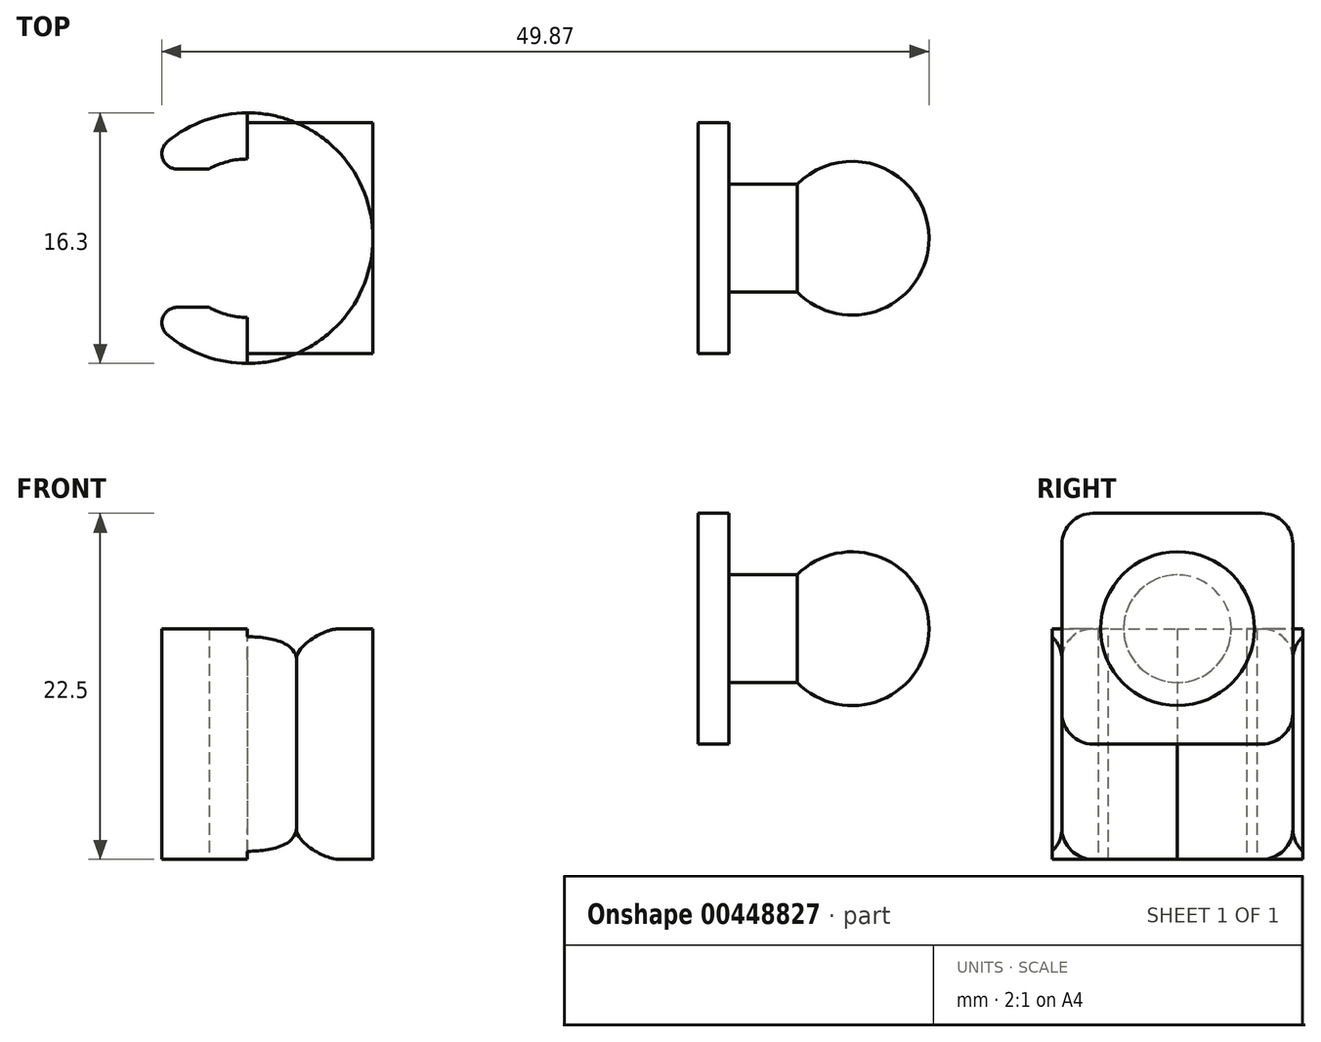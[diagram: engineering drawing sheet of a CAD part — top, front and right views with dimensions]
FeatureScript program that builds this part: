
annotation { "Feature Type Name" : "Feature", "Feature Type Description" : "" }
export const myFeature = defineFeature(function(context is Context, id is Id, definition is map)
    precondition{}
    {
        {
            var Q0;
            Q0=qCreatedBy(makeId("Top.planeOp"),FACE);
            var sketch = newSketch(context, id + "F0", { "sketchPlane" : qUnion([Q0])});
            skLineSegment(sketch, "E0.bottom", {"start": v(0, 0) * mm, "end": v(-8.15, 0) * mm});
            skLineSegment(sketch, "E0.top", {"start": v(0, 15) * mm, "end": v(-8.15, 15) * mm});
            skLineSegment(sketch, "E0.left", {"start": v(0, 0) * mm, "end": v(0, 15) * mm});
            skLineSegment(sketch, "E0.right", {"start": v(-8.15, 0) * mm, "end": v(-8.15, 15) * mm});
            skCircle(sketch, "E1", {"center": v(-8.15, 7.5) * mm, "radius": 8.15 * mm});
            skPoint(sketch, "E1.centerSnap0", {"position": v(-8.15, 7.5) * mm});
            skCircle(sketch, "E2", {"center": v(-8.15, 7.5) * mm, "radius": 5.15 * mm});
            skLineSegment(sketch, "E3.bottom", {"start": v(-22.3, 12) * mm, "end": v(-10.3, 12) * mm});
            skLineSegment(sketch, "E3.top", {"start": v(-22.3, 3) * mm, "end": v(-10.3, 3) * mm});
            skLineSegment(sketch, "E3.left", {"start": v(-22.3, 12) * mm, "end": v(-22.3, 3) * mm});
            skLineSegment(sketch, "E3.right", {"start": v(-10.3, 12) * mm, "end": v(-10.3, 3) * mm});
            skPoint(sketch, "E3.middle", {"position": v(-16.3, 7.5) * mm});
            skSolve(sketch);
        }
        {
            var Q0;
            {var subQ1=sQuery(id+"F0.wireOp",EDGE,"E0.right");var subQ6=sQuery(id+"F0.wireOp",EDGE,"E0.top");var subQ9=makeQuery(id+"F0.imprint","INTERSECT",VERTEX,{"derivedFrom":[subQ6,subQ1]});Q0=makeQuery(id+"F0.imprint","IMPRINT",FACE,{"disambiguationData":[TD([[makeQuery(id+"F0.imprint","IMPRINT",EDGE,{"disambiguationData":[TD([[subQ9,1.0]])],"derivedFrom":subQ6}),-1.0]])]});}
            var Q1;
            {var subQ3=sQuery(id+"F0.wireOp",EDGE,"E2");var subQ6=makeQuery(id+"F0.imprint","IMPRINT",VERTEX,{"derivedFrom":subQ3});Q1=makeQuery(id+"F0.imprint","IMPRINT",FACE,{"disambiguationData":[TD([[makeQuery(id+"F0.imprint","IMPRINT",EDGE,{"disambiguationData":[TD([[subQ6,-1.0]])],"derivedFrom":subQ3}),-1.0]])]});}
            var Q2;
            {var subQ1=sQuery(id+"F0.wireOp",EDGE,"E0.right");var subQ6=sQuery(id+"F0.wireOp",EDGE,"E0.bottom");var subQ9=makeQuery(id+"F0.imprint","INTERSECT",VERTEX,{"derivedFrom":[subQ6,subQ1]});Q2=makeQuery(id+"F0.imprint","IMPRINT",FACE,{"disambiguationData":[TD([[makeQuery(id+"F0.imprint","IMPRINT",EDGE,{"disambiguationData":[TD([[subQ9,1.0]])],"derivedFrom":subQ6}),1.0]])]});}
            var Q3;
            {var subQ0=sQuery(id+"F0.wireOp",EDGE,"E0.left");var subQ1=sQuery(id+"F0.wireOp",EDGE,"E0.bottom");var subQ2=makeQuery(id+"F0.imprint","INTERSECT",VERTEX,{"derivedFrom":[subQ1,subQ0]});Q3=makeQuery(id+"F0.imprint","IMPRINT",FACE,{"disambiguationData":[TD([[makeQuery(id+"F0.imprint","IMPRINT",EDGE,{"disambiguationData":[TD([[subQ2,-1.0]])],"derivedFrom":subQ1}),-1.0]])]});}
            var Q4;
            {var subQ0=sQuery(id+"F0.wireOp",EDGE,"E0.left");var subQ1=sQuery(id+"F0.wireOp",EDGE,"E0.top");var subQ2=makeQuery(id+"F0.imprint","INTERSECT",VERTEX,{"derivedFrom":[subQ1,subQ0]});Q4=makeQuery(id+"F0.imprint","IMPRINT",FACE,{"disambiguationData":[TD([[makeQuery(id+"F0.imprint","IMPRINT",EDGE,{"disambiguationData":[TD([[subQ2,-1.0]])],"derivedFrom":subQ1}),1.0]])]});}
            extrude(context, id + "F1", {"entities" : qUnion([Q0, Q1, Q2, Q3, Q4]), "depth" : 15 * mm, "offsetDistance" : 25 * mm});
        }
        {
            var Q0;
            Q0=makeQuery(id+"F1.opExtrude","SWEPT_EDGE",EDGE,{"disambiguationData":[OSD([sQuery(id+"F0.wireOp",EDGE,"E1"),sQuery(id+"F0.wireOp",EDGE,"E3.bottom")])]});
            var Q1;
            Q1=makeQuery(id+"F1.opExtrude","SWEPT_EDGE",EDGE,{"disambiguationData":[OSD([sQuery(id+"F0.wireOp",EDGE,"E1"),sQuery(id+"F0.wireOp",EDGE,"E3.top")])]});
            fillet(context, id + "F2", {"entities" : qUnion([Q0, Q1]), "tangentPropagation" : true, "radius" : 1 * mm, "defaultsChanged" : true, "vertexSettings" : [], "allowEdgeOverflow" : false});
        }
        {
            var Q0;
            Q0=makeQuery(id+"F1.opExtrude","CAP_FACE",FACE,{"disambiguationData":[OSD([sQuery(id+"F0.wireOp",EDGE,"E0.bottom"),sQuery(id+"F0.wireOp",EDGE,"E0.top"),sQuery(id+"F0.wireOp",EDGE,"E0.left"),sQuery(id+"F0.wireOp",EDGE,"E1"),sQuery(id+"F0.wireOp",EDGE,"E2"),sQuery(id+"F0.wireOp",EDGE,"E3.bottom"),sQuery(id+"F0.wireOp",EDGE,"E3.top")])],"isStart":false});
            var sketch = newSketch(context, id + "F3", { "sketchPlane" : qUnion([Q0])});
            skLineSegment(sketch, "E4.bottom", {"start": v(21.15, 0) * mm, "end": v(23.15, 0) * mm});
            skLineSegment(sketch, "E4.top", {"start": v(21.15, 15) * mm, "end": v(23.15, 15) * mm});
            skLineSegment(sketch, "E4.left", {"start": v(21.15, 0) * mm, "end": v(21.15, 15) * mm});
            skLineSegment(sketch, "E4.right", {"start": v(23.15, 0) * mm, "end": v(23.15, 15) * mm});
            skLineSegment(sketch, "E5.bottom", {"start": v(23.15, 11) * mm, "end": v(31.15, 11) * mm});
            skLineSegment(sketch, "E5.top", {"start": v(23.15, 4) * mm, "end": v(31.15, 4) * mm});
            skLineSegment(sketch, "E5.left", {"start": v(23.15, 11) * mm, "end": v(23.15, 4) * mm});
            skLineSegment(sketch, "E5.right", {"start": v(31.15, 11) * mm, "end": v(31.15, 4) * mm});
            skPoint(sketch, "E5.middle", {"position": v(27.15, 7.5) * mm});
            skPoint(sketch, "E5.middle.positionSnap0", {"position": v(23.15, 7.5) * mm});
            skPoint(sketch, "E5.centerSnap0", {"position": v(23.15, 7.5) * mm});
            skCircle(sketch, "E6", {"center": v(31.15, 7.5) * mm, "radius": 5 * mm});
            skLineSegment(sketch, "E7", {"start": v(17.75, 7.5) * mm, "end": v(39.24, 7.5) * mm});
            skPoint(sketch, "E7.startSnap0", {"position": v(21.15, 7.5) * mm});
            skSolve(sketch);
        }
        {
            var Q0;
            {var subQ1=sQuery(id+"F3.wireOp",EDGE,"E4.top");Q0=makeQuery(id+"F3.imprint","IMPRINT",FACE,{"disambiguationData":[TD([[makeQuery(id+"F3.imprint","IMPRINT",EDGE,{"derivedFrom":subQ1}),-1.0]])]});}
            var Q1;
            {var subQ0=sQuery(id+"F3.wireOp",EDGE,"E5.bottom");var subQ1=sQuery(id+"F3.wireOp",EDGE,"E4.right");var subQ2=makeQuery(id+"F3.imprint","INTERSECT",VERTEX,{"derivedFrom":[subQ1,subQ0]});Q1=makeQuery(id+"F3.imprint","IMPRINT",FACE,{"disambiguationData":[TD([[makeQuery(id+"F3.imprint","IMPRINT",EDGE,{"disambiguationData":[TD([[subQ2,1.0]])],"derivedFrom":subQ1}),-1.0]])]});}
            var Q2;
            {var subQ0=sQuery(id+"F3.wireOp",EDGE,"E5.right");var subQ1=sQuery(id+"F3.wireOp",EDGE,"E5.bottom");var subQ2=makeQuery(id+"F3.imprint","INTERSECT",VERTEX,{"derivedFrom":[subQ1,subQ0]});Q2=makeQuery(id+"F3.imprint","IMPRINT",FACE,{"disambiguationData":[TD([[makeQuery(id+"F3.imprint","IMPRINT",EDGE,{"disambiguationData":[TD([[subQ2,1.0]])],"derivedFrom":subQ1}),-1.0]])]});}
            var Q3;
            {var subQ0=sQuery(id+"F3.wireOp",EDGE,"E5.right");var subQ1=sQuery(id+"F3.wireOp",EDGE,"E5.bottom");var subQ2=makeQuery(id+"F3.imprint","INTERSECT",VERTEX,{"derivedFrom":[subQ1,subQ0]});Q3=makeQuery(id+"F3.imprint","IMPRINT",FACE,{"disambiguationData":[TD([[makeQuery(id+"F3.imprint","IMPRINT",EDGE,{"disambiguationData":[TD([[subQ2,1.0]])],"derivedFrom":subQ1}),1.0]])]});}
            var Q4;
            Q4=sQuery(id+"F3.wireOp",EDGE,"E7");
            revolve(context, id + "F4", {"surfaceOperationType" : NewSurfaceOperationType.NEW, "entities" : qUnion([Q0, Q1, Q2, Q3]), "axis" : qUnion([Q4]), "revolveType" : RevolveType.FULL});
        }
        {
            var Q0;
            Q0=makeQuery(id+"F4.opRevolve","SWEPT_FACE",FACE,{"disambiguationData":[OSD([sQuery(id+"F3.wireOp",EDGE,"E4.left")])]});
            var sketch = newSketch(context, id + "F5", { "sketchPlane" : qUnion([Q0])});
            skLineSegment(sketch, "E8.bottom", {"start": v(-15, 7.5) * mm, "end": v(0, 7.5) * mm});
            skLineSegment(sketch, "E8.top", {"start": v(-15, 22.5) * mm, "end": v(0, 22.5) * mm});
            skLineSegment(sketch, "E8.left", {"start": v(-15, 7.5) * mm, "end": v(-15, 22.5) * mm});
            skLineSegment(sketch, "E8.right", {"start": v(0, 7.5) * mm, "end": v(0, 22.5) * mm});
            skPoint(sketch, "E8.middle", {"position": v(-7.5, 15) * mm});
            skSolve(sketch);
        }
        {
            var Q0;
            {var subQ0=sQuery(id+"F5.wireOp",EDGE,"E8.left");var subQ1=sQuery(id+"F5.wireOp",EDGE,"E8.bottom");var subQ2=makeQuery(id+"F5.imprint","INTERSECT",VERTEX,{"derivedFrom":[subQ1,subQ0]});Q0=makeQuery(id+"F5.imprint","IMPRINT",FACE,{"disambiguationData":[TD([[makeQuery(id+"F5.imprint","IMPRINT",EDGE,{"disambiguationData":[TD([[subQ2,-1.0]])],"derivedFrom":subQ1}),1.0]])]});}
            var Q1;
            {var subQ0=sQuery(id+"F5.wireOp",EDGE,"E8.left");var subQ1=sQuery(id+"F5.wireOp",EDGE,"E8.top");var subQ2=makeQuery(id+"F5.imprint","INTERSECT",VERTEX,{"derivedFrom":[subQ1,subQ0]});Q1=makeQuery(id+"F5.imprint","IMPRINT",FACE,{"disambiguationData":[TD([[makeQuery(id+"F5.imprint","IMPRINT",EDGE,{"disambiguationData":[TD([[subQ2,-1.0]])],"derivedFrom":subQ1}),-1.0]])]});}
            var Q2;
            {var subQ0=sQuery(id+"F5.wireOp",EDGE,"E8.right");var subQ1=sQuery(id+"F5.wireOp",EDGE,"E8.top");var subQ2=makeQuery(id+"F5.imprint","INTERSECT",VERTEX,{"derivedFrom":[subQ1,subQ0]});Q2=makeQuery(id+"F5.imprint","IMPRINT",FACE,{"disambiguationData":[TD([[makeQuery(id+"F5.imprint","IMPRINT",EDGE,{"disambiguationData":[TD([[subQ2,1.0]])],"derivedFrom":subQ1}),-1.0]])]});}
            var Q3;
            {var subQ0=sQuery(id+"F5.wireOp",EDGE,"E8.right");var subQ1=sQuery(id+"F5.wireOp",EDGE,"E8.bottom");var subQ2=makeQuery(id+"F5.imprint","INTERSECT",VERTEX,{"derivedFrom":[subQ1,subQ0]});Q3=makeQuery(id+"F5.imprint","IMPRINT",FACE,{"disambiguationData":[TD([[makeQuery(id+"F5.imprint","IMPRINT",EDGE,{"disambiguationData":[TD([[subQ2,1.0]])],"derivedFrom":subQ1}),1.0]])]});}
            extrude(context, id + "F6", {"entities" : qUnion([Q0, Q1, Q2, Q3]), "operationType" : NewBodyOperationType.ADD, "oppositeDirection" : true, "depth" : 2 * mm, "offsetDistance" : 25 * mm});
        }
        {
            var Q0;
            Q0=makeQuery(id+"F6.opExtrude","SWEPT_EDGE",EDGE,{"disambiguationData":[OSD([sQuery(id+"F5.wireOp",EDGE,"E8.top"),sQuery(id+"F5.wireOp",EDGE,"E8.left")])]});
            var Q1;
            Q1=makeQuery(id+"F6.opExtrude","SWEPT_EDGE",EDGE,{"disambiguationData":[OSD([sQuery(id+"F5.wireOp",EDGE,"E8.bottom"),sQuery(id+"F5.wireOp",EDGE,"E8.left")])]});
            var Q2;
            Q2=makeQuery(id+"F6.opExtrude","SWEPT_EDGE",EDGE,{"disambiguationData":[OSD([sQuery(id+"F5.wireOp",EDGE,"E8.bottom"),sQuery(id+"F5.wireOp",EDGE,"E8.right")])]});
            var Q3;
            Q3=makeQuery(id+"F6.opExtrude","SWEPT_EDGE",EDGE,{"disambiguationData":[OSD([sQuery(id+"F5.wireOp",EDGE,"E8.top"),sQuery(id+"F5.wireOp",EDGE,"E8.right")])]});
            var Q4;
            Q4=makeQuery(id+"F1.opExtrude","CAP_EDGE",EDGE,{"disambiguationData":[OSD([sQuery(id+"F0.wireOp",EDGE,"E0.bottom")])],"isStart":true});
            var Q5;
            Q5=makeQuery(id+"F1.opExtrude","CAP_EDGE",EDGE,{"disambiguationData":[OSD([sQuery(id+"F0.wireOp",EDGE,"E0.top")])],"isStart":true});
            var Q6;
            Q6=makeQuery(id+"F1.opExtrude","CAP_EDGE",EDGE,{"disambiguationData":[OSD([sQuery(id+"F0.wireOp",EDGE,"E0.top")])],"isStart":false});
            var Q7;
            Q7=makeQuery(id+"F1.opExtrude","CAP_EDGE",EDGE,{"disambiguationData":[OSD([sQuery(id+"F0.wireOp",EDGE,"E0.bottom")])],"isStart":false});
            fillet(context, id + "F7", {"entities" : qUnion([Q0, Q1, Q2, Q3, Q4, Q5, Q6, Q7]), "tangentPropagation" : true, "radius" : 2 * mm, "defaultsChanged" : false, "vertexSettings" : [], "allowEdgeOverflow" : false});
        }
    });
